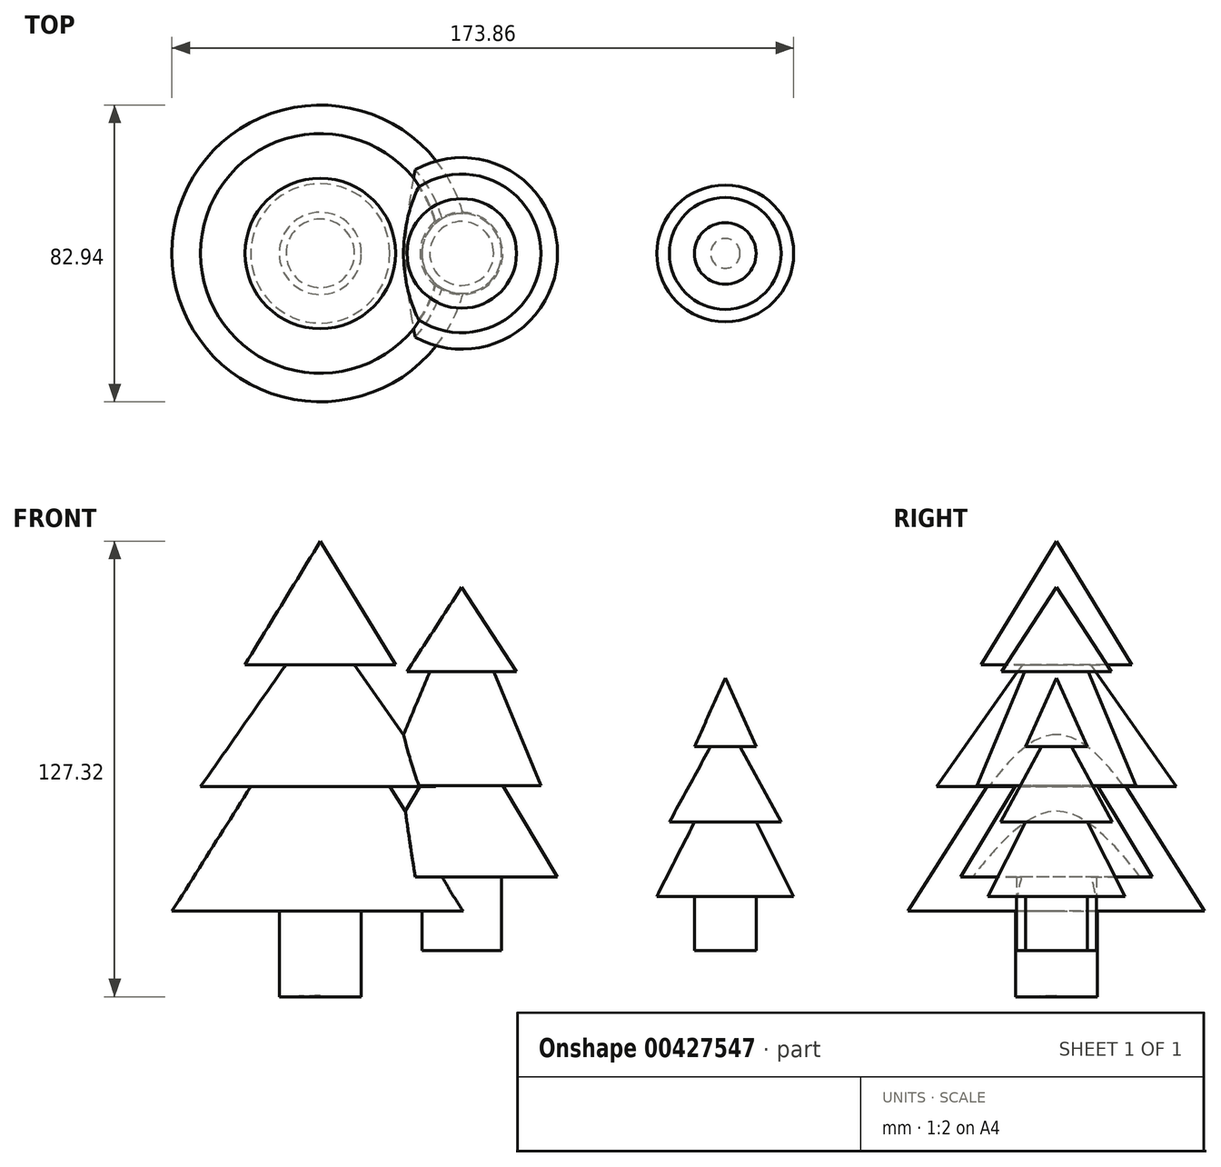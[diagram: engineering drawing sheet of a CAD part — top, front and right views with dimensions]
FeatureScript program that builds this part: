
annotation { "Feature Type Name" : "Feature", "Feature Type Description" : "" }
export const myFeature = defineFeature(function(context is Context, id is Id, definition is map)
    precondition{}
    {
        {
            var Q0;
            Q0=qCreatedBy(makeId("Front.planeOp"),FACE);
            var sketch = newSketch(context, id + "F0", { "sketchPlane" : qUnion([Q0])});
            skLineSegment(sketch, "E0", {"start": v(-61.73, -12.6) * mm, "end": v(-61.73, 114.4) * mm});
            skLineSegment(sketch, "E1", {"start": v(-61.73, 114.4) * mm, "end": v(-82.79, 79.91) * mm});
            skLineSegment(sketch, "E2", {"start": v(-82.79, 79.91) * mm, "end": v(-71.3, 79.91) * mm});
            skLineSegment(sketch, "E3", {"start": v(-71.3, 79.91) * mm, "end": v(-95.23, 45.78) * mm});
            skLineSegment(sketch, "E4", {"start": v(-95.23, 45.78) * mm, "end": v(-81.2, 45.78) * mm});
            skLineSegment(sketch, "E5", {"start": v(-81.2, 45.78) * mm, "end": v(-103.2, 11) * mm});
            skLineSegment(sketch, "E6", {"start": v(-103.2, 11) * mm, "end": v(-73.21, 11) * mm});
            skLineSegment(sketch, "E7", {"start": v(-73.21, 11) * mm, "end": v(-73.21, -12.92) * mm});
            skLineSegment(sketch, "E8", {"start": v(-73.21, -12.92) * mm, "end": v(-61.73, -12.6) * mm});
            skLineSegment(sketch, "E9", {"start": v(-22.17, 0) * mm, "end": v(-22.17, 101.6) * mm});
            skLineSegment(sketch, "E10", {"start": v(-22.17, 101.6) * mm, "end": v(-6.86, 78) * mm});
            skLineSegment(sketch, "E11", {"start": v(-6.86, 78) * mm, "end": v(-13.24, 78) * mm});
            skLineSegment(sketch, "E12", {"start": v(-13.24, 78) * mm, "end": v(0, 46.1) * mm});
            skLineSegment(sketch, "E13", {"start": v(0, 46.1) * mm, "end": v(-10.69, 46.1) * mm});
            skLineSegment(sketch, "E14", {"start": v(-10.69, 46.1) * mm, "end": v(4.63, 20.58) * mm});
            skLineSegment(sketch, "E15", {"start": v(4.63, 20.58) * mm, "end": v(-11, 20.58) * mm});
            skLineSegment(sketch, "E16", {"start": v(-11, 20.58) * mm, "end": v(-11, 0) * mm});
            skLineSegment(sketch, "E17", {"start": v(-11, 0) * mm, "end": v(-22.17, 0) * mm});
            skLineSegment(sketch, "E18", {"start": v(51.52, 0) * mm, "end": v(51.52, 76.2) * mm});
            skLineSegment(sketch, "E19", {"start": v(51.52, 76.2) * mm, "end": v(60.13, 56.94) * mm});
            skLineSegment(sketch, "E20", {"start": v(60.13, 56.94) * mm, "end": v(55.67, 56.94) * mm});
            skLineSegment(sketch, "E21", {"start": v(55.67, 56.94) * mm, "end": v(67.15, 35.89) * mm});
            skLineSegment(sketch, "E22", {"start": v(67.15, 35.89) * mm, "end": v(60.13, 35.89) * mm});
            skLineSegment(sketch, "E23", {"start": v(60.13, 35.89) * mm, "end": v(70.66, 15.15) * mm});
            skLineSegment(sketch, "E24", {"start": v(70.66, 15.15) * mm, "end": v(60.13, 15.15) * mm});
            skLineSegment(sketch, "E25", {"start": v(60.13, 15.15) * mm, "end": v(60.13, 0) * mm});
            skLineSegment(sketch, "E26", {"start": v(60.13, 0) * mm, "end": v(51.52, 0) * mm});
            skSolve(sketch);
        }
        {
            var Q0;
            Q0=makeQuery(id+"F0.imprint","IMPRINT",FACE,{"disambiguationData":[TD([[makeQuery(id+"F0.imprint","IMPRINT",EDGE,{"derivedFrom":sQuery(id+"F0.wireOp",EDGE,"E0")}),1.0]])]});
            var Q1;
            Q1=sQuery(id+"F0.wireOp",EDGE,"E0");
            revolve(context, id + "F1", {"entities" : qUnion([Q0]), "axis" : qUnion([Q1]), "revolveType" : RevolveType.FULL});
        }
        {
            var Q0;
            Q0=makeQuery(id+"F0.imprint","IMPRINT",FACE,{"disambiguationData":[TD([[makeQuery(id+"F0.imprint","IMPRINT",EDGE,{"derivedFrom":sQuery(id+"F0.wireOp",EDGE,"E9")}),-1.0]])]});
            var Q1;
            Q1=sQuery(id+"F0.wireOp",EDGE,"E9");
            revolve(context, id + "F2", {"operationType" : NewBodyOperationType.ADD, "entities" : qUnion([Q0]), "axis" : qUnion([Q1]), "revolveType" : RevolveType.FULL});
        }
        {
            var Q0;
            Q0=makeQuery(id+"F0.imprint","IMPRINT",FACE,{"disambiguationData":[TD([[makeQuery(id+"F0.imprint","IMPRINT",EDGE,{"derivedFrom":sQuery(id+"F0.wireOp",EDGE,"E18")}),-1.0]])]});
            var Q1;
            Q1=sQuery(id+"F0.wireOp",EDGE,"E18");
            revolve(context, id + "F3", {"entities" : qUnion([Q0]), "axis" : qUnion([Q1]), "revolveType" : RevolveType.FULL});
        }
    });
